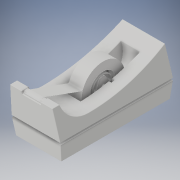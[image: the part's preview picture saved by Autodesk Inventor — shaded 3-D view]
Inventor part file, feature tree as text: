
AUTODESK INVENTOR PART (.ipt)
format: ipt  version: 2017 (Build 210142000, 142)  size: 640,000 bytes
history: native  units: in
note: dims shown in document units (in); Inventor stores cm internally (conversion verified against a paired STEP export)
features: sketch x11, extrude x10, other x4, mirror x1, fillet x1
ambient origin geometry x8: Origin, YZ Plane, XZ Plane, XY Plane, X Axis, Y Axis, Z Axis, Center Point
bodies: Solid1 (feature_tree), Solid2 (feature_tree)
feature tree (27):
  extrude  "side view"  Depth=0.0063in
  extrude  "front view"  Depth=0.1374in
  extrude  "tape gap"  Depth=0.011in
  extrude  "tape holder rack"  Depth=0.1372in
  mirror  "mirror tape holder rack"
  other  "axle for tape workplane"
  other  "axle for tape"
  extrude  "tape holder"  Depth=0.353in
  sketch  "Sketch8"  dims[d11=0.0889in d12=0.2191in d13=0.0in]
  other  "tape ring"
  other  "tape"
  extrude  "inner of cutter"  Depth=0.2191in TaperAngle=0.0deg
  extrude  "middle of cutter"  Depth=0.1382in
  extrude  "outer of cutter"  Depth=0.5774in
  extrude  "cutting teeth"  Depth=0.0672in
  extrude  "tap to cutter"  Depth=0.1409in
  fillet  "smooth edges"  Radius=0.0698in
  sketch  "Sketch1"  dims[d1=0.0723in d2=0.0063in]
  sketch  "Sketch2"  dims[d3=0.0107in d4=0.1374in]
  sketch  "Sketch3"  dims[d5=0.1392in d6=0.011in]
  sketch  "Sketch4"  dims[d7=0.4882in d8=0.1372in]
  sketch  "Sketch5"  dims[d9=0.032in d10=0.353in]
  sketch  "Sketch10"  dims[d14=0.4882in d15=0.1382in]
  sketch  "Sketch11"  dims[d17=0.5774in d18=0.5774in]
  sketch  "Sketch12"  dims[d19=0.2191in d20=0.0in d21=0.0672in]
  sketch  "Sketch13"  dims[d22=0.2719in d23=0.1409in d24=0.0698in]
  sketch  "Sketch14"  dims[d25=0.0128in d28=0.0113in d30=0.0845in d31=0.0in d32=0.1267in d33=0.0105in d34=0.0063in d35=0.006in d36=0.018in d38=0.0234in d39=0.0388in d40=0.0125in d41=0.0in d42=0.0117in d44=0.1071in d45=0.008in d48=0.009in d49=90.0deg d53=0.0308in d54=0.0098in d55=0.052in d57=0.0798in d58=0.0745in d59=0.0405in d61=0.0126in d62=0.0126in d67=0.0387in d68=0.0618in d69=0.0in d70=0.043in d71=0.043in d73=0.0298in d74=0.0112in d75=0.0028in d76=0.0028in d77=0.0366in d81=90.0deg d82=90.0deg d87=0.0295in d88=0.011in d89=0.001in d90=0.0149in d91=0.0034in d93=0.0047in d94=0.0145in d96=0.0052in d97=0.0035in d98=0.0054in d99=0.0027in d100=0.0048in d101=0.0048in d102=0.0023in d103=0.0371in d104=0.0in d107=0.0238in d108=0.0778in d109=0.0in d110=0.003in d111=0.0053in d112=0.0858in d113=0.0in d114=0.0858in d115=0.0034in d117=0.0018in d154=0.0858in d155=0.0in d156=0.028in d157=0.0003in d159=0.0062in d160=0.0003in d161=0.0618in d162=0.0in d163=0.0618in d164=0.002in d165=0.011in d166=0.011in]
